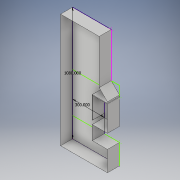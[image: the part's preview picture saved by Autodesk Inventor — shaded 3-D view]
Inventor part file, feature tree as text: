
AUTODESK INVENTOR PART (.ipt)
format: ipt  version: 2017 (Build 210142000, 142)  size: 148,992 bytes
history: native  units: in
note: dims shown in document units (in); Inventor stores cm internally (conversion verified against a paired STEP export)
features: sketch x4, extrude x3, plane x1, chamfer x1, shell x1
ambient origin geometry x8: Origin, YZ Plane, XZ Plane, XY Plane, X Axis, Y Axis, Z Axis, Center Point
bodies: Body1 (feature_tree)
feature tree (10):
  sketch  "Sketch1"  dims[d0=1080.0in d1=300.0in d5=114.0in d6=0.0in]
  plane  "Work Plane1"
  sketch  "Sketch2"  dims[d7=78.0in d8=0.125in d9=45.0deg d10=114.0in d11=0.0in d12=0.1in]
  extrude  "Extrusion2"  Depth=300.0in
  chamfer  "Chamfer1"  Distance=114.0in
  extrude  "Extrusion3"  Depth=114.0in TaperAngle=0.0deg
  shell  "Shell2"  Thickness=0.1in
  extrude  "Extrusion4"  Depth=114.0in TaperAngle=0.0deg
  sketch  "Sketch3"  dims[d13=1.0in d14=114.0in d15=0.0in]
  sketch  "Sketch4"
